SOLIDWORKS PART (.sldprt)
format: sldprt  version: not decoded by parser v0  size: 48,640 bytes
history: native  units: mm
features: sketch x3, extrude x3 + 2 further entries (+8 scaffold rows collapsed; 3 parser-record rows omitted)
feature tree (19):
  scaffold x8  (default folders/planes/origin — collapsed)
  parser-record x3  (decoder bookkeeping rows leaked as tree rows — omitted from the tree; the rows remain in map.json)
  "ID2"
  "ID3"
  sketch  "Sketch1"  dims[D1=~8.17626mm]
  extrude  "Base-Extrude"  Depth=5.08mm
  sketch  "Sketch2"  dims[D1=5.08mm]
  extrude  "Boss-Extrude1"  Depth=32.766mm
  sketch  "Sketch3"
  extrude  "Boss-Extrude2"  Depth=5.08mm
decode coverage: 5 of 6 modeling features carry decoded parameters; 2 rows unclassified (native names shown)
note: ~ marks probable driven/reference dimensions
note: suppression state not decoded; provenance and decode notes live in map.json
